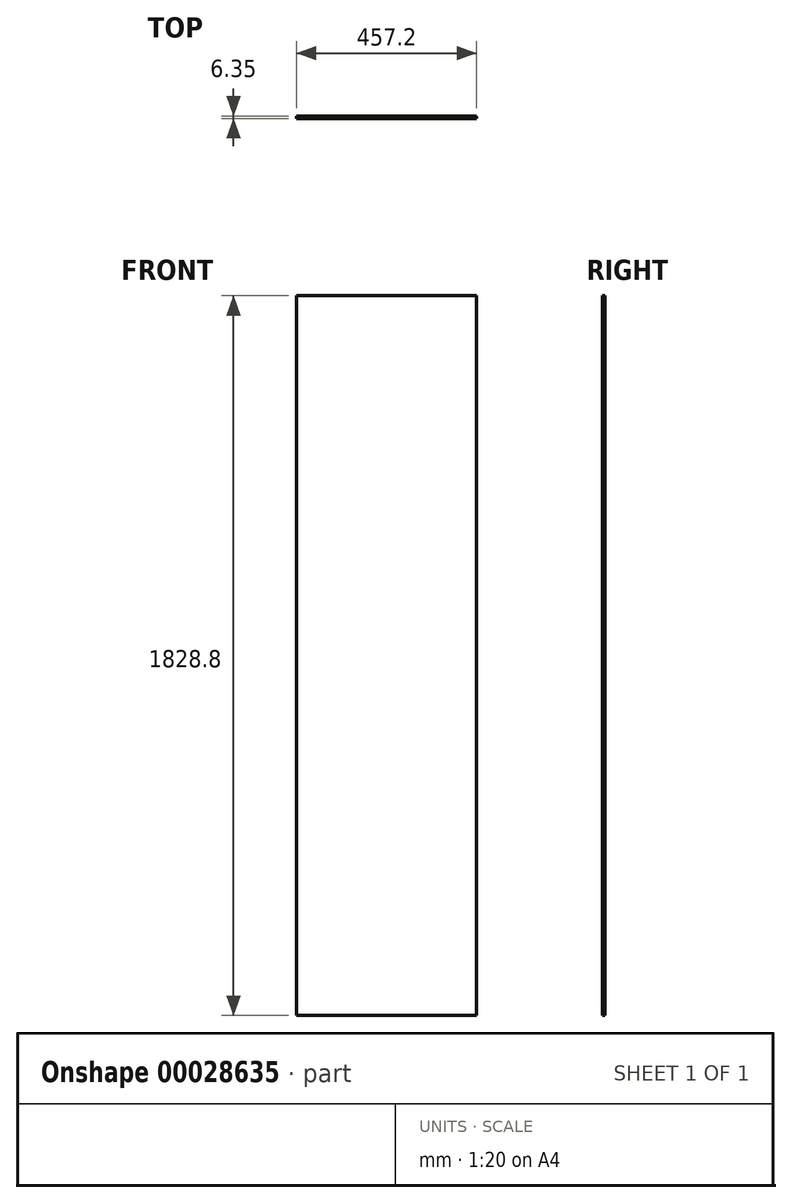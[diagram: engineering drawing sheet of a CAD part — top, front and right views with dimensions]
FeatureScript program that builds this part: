
annotation { "Feature Type Name" : "Feature", "Feature Type Description" : "" }
export const myFeature = defineFeature(function(context is Context, id is Id, definition is map)
    precondition{}
    {
        {
            var Q0;
            Q0=qCreatedBy(makeId("Front.planeOp"),FACE);
            var sketch = newSketch(context, id + "F0", { "sketchPlane" : qUnion([Q0])});
            skLineSegment(sketch, "E0.rect.bottom", {"start": v(228.6, -914.4) * mm, "end": v(-228.6, -914.4) * mm});
            skLineSegment(sketch, "E0.rect.top", {"start": v(228.6, 914.4) * mm, "end": v(-228.6, 914.4) * mm});
            skLineSegment(sketch, "E0.rect.left", {"start": v(228.6, -914.4) * mm, "end": v(228.6, 914.4) * mm});
            skLineSegment(sketch, "E0.rect.right", {"start": v(-228.6, -914.4) * mm, "end": v(-228.6, 914.4) * mm});
            skPoint(sketch, "E0.rect.middle", {"position": v(0, 0) * mm});
            skSolve(sketch);
        }
        {
            var Q0;
            Q0 = qSketchRegion(id + "F0", true);
            extrude(context, id + "F1", {"entities" : qUnion([Q0]), "depth" : 6.35 * mm});
        }
    });
